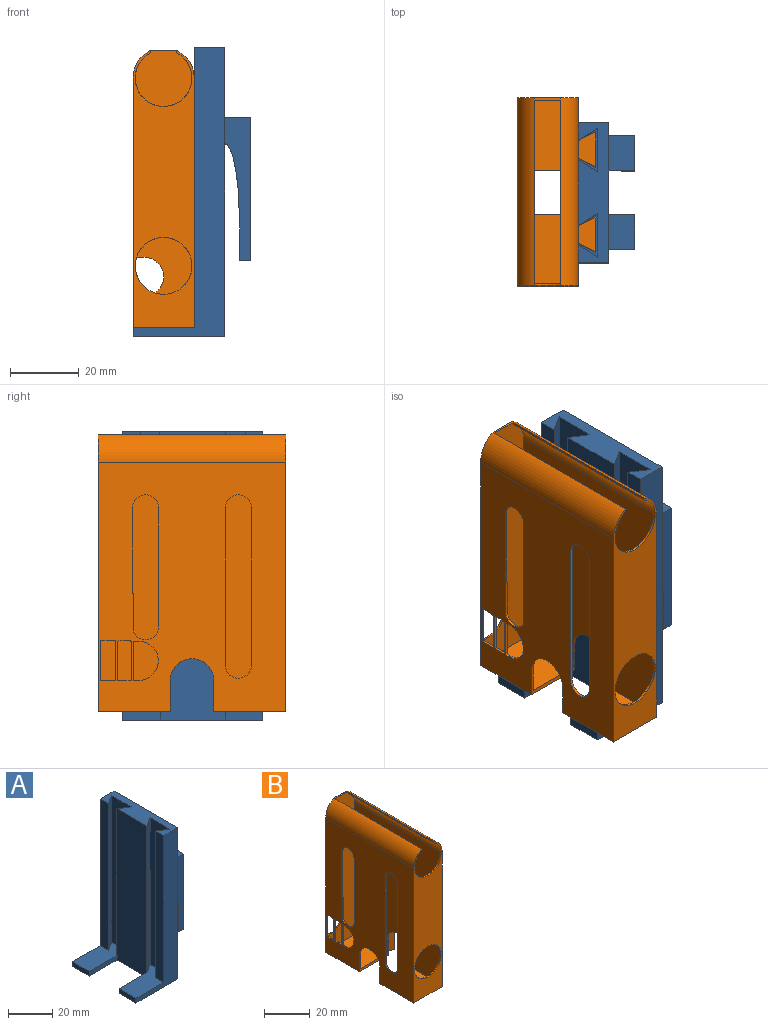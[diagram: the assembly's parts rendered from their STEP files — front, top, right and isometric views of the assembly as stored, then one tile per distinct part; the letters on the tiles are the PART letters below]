
ASSEMBLY  parts=2 mates=1
PART A: 34 faces, bbox 34.3x40.6x83.8 mm
  f0: plane 40.64x26.67mm, normal (0,0,-1), area 745.2mm2, adj f2,f5,f9,f18,f19,f20,f32,f33
  f1: plane 23.37x14.29mm, normal (0,0,1), area 243mm2, adj f2,f3,f9,f14,f15,f16,f20,f33
  f2: plane 10.8x2.54mm, normal (-1,0,0), area 27.4mm2, adj f0,f1,f20,f33
  f3: plane 81.28x5.14mm, normal (-1,0,0), area 418.1mm2, adj f1,f4,f14,f33
  f4: plane 40.64x8.89mm, normal (0,0,1), area 259.1mm2, adj f3,f5,f9,f10,f11,f12,f13,f14
  f5: plane 83.82x40.64mm, normal (1,0,0), area 3251.7mm2, adj f0,f4,f6,f7,f8,f21,f22,f24
  f6: plane 41.59x7.62mm, normal (0,1,0), area 190.3mm2, adj f5,f21,f23,f29,f30,f31
  f7: plane 41.59x7.62mm, normal (0,-1,0), area 190.3mm2, adj f5,f24,f25,f26,f27,f28
  f8: plane 41.59x7.62mm, normal (0,1,0), area 190.3mm2, adj f5,f24,f25,f26,f27,f28
  f9: plane 83.82x19.18mm, normal (-1,0,0), area 1607.1mm2, adj f0,f1,f4,f13,f15,f17,f19,f20
  f10: plane 81.28x5.14mm, normal (-1,0,0), area 418.1mm2, adj f4,f11,f17,f32
  f11: plane 81.28x5.59mm, normal (0.54,0.84,0), area 538.4mm2, adj f4,f10,f12,f17
  f12: plane 81.28x12.7mm, normal (-1,0,0), area 1032.3mm2, adj f4,f11,f13,f17
  f13: plane 81.28x5.59mm, normal (0.54,-0.84,0), area 538.4mm2, adj f4,f9,f12,f17
  f14: plane 81.28x5.59mm, normal (0.54,-0.84,0), area 538.4mm2, adj f1,f3,f4,f16
  f15: plane 81.28x5.59mm, normal (0.54,0.84,0), area 538.4mm2, adj f1,f4,f9,f16
  f16: plane 81.28x12.7mm, normal (-1,0,0), area 1032.3mm2, adj f1,f4,f14,f15
  f17: plane 23.37x14.29mm, normal (0,0,1), area 243mm2, adj f9,f10,f11,f12,f13,f18,f19,f32
  f18: plane 10.8x2.54mm, normal (-1,0,0), area 27.4mm2, adj f0,f17,f19,f32
  f19: plane 17.78x2.54mm, normal (0,1,0), area 45.2mm2, adj f0,f9,f17,f18
  f20: plane 17.78x2.54mm, normal (0,-1,0), area 45.2mm2, adj f0,f1,f2,f9
  f21: plane 10.16x7.62mm, normal (0,0,1), area 77.4mm2, adj f5,f6,f22,f23
  f22: plane 41.59x7.62mm, normal (0,-1,0), area 190.3mm2, adj f5,f21,f23,f29,f30,f31
  f23: plane 41.59x10.16mm, normal (1,0,0), area 422.6mm2, adj f6,f21,f22,f29
  f24: plane 10.16x7.62mm, normal (0,0,1), area 77.4mm2, adj f5,f7,f8,f25
  f25: plane 41.59x10.16mm, normal (1,0,0), area 422.6mm2, adj f7,f8,f24,f28
  f26: extruded ~24.13x10.16mm, area 255.8mm2, adj f5,f7,f8,f27
  f27: plane 10.16x9.84mm, normal (-1,0,0), area 100mm2, adj f7,f8,f26,f28
  f28: plane 10.16x3.22mm, normal (0,0,-1), area 32.7mm2, adj f7,f8,f25,f27
  f29: plane 10.16x3.22mm, normal (0,0,-1), area 32.7mm2, adj f6,f22,f23,f30
  f30: plane 10.16x9.84mm, normal (-1,0,0), area 100mm2, adj f6,f22,f29,f31
  f31: extruded ~24.13x10.16mm, area 255.8mm2, adj f5,f6,f22,f30
  f32: plane 83.82x26.67mm, normal (0,-1,0), area 790.3mm2, adj f0,f4,f5,f10,f17,f18
  f33: plane 83.82x26.67mm, normal (0,1,0), area 790.3mm2, adj f0,f1,f2,f3,f4,f5
PART B: 58 faces, bbox 22.9x54.6x80.4 mm
  f0: plane 72.39x54.61mm, normal (-1,0,0), area 2911mm2, adj f1,f2,f3,f4,f6,f7,f8,f9
  f1: plane 3.89x0.64mm, normal (0,0,1), area 2.5mm2, adj f0,f13,f51,f54
  f2: plane 1.56x0.64mm, normal (0,0,-1), area 1mm2, adj f0,f13,f47,f55
  f3: cylinder r=3.81mm len=7.42mm, axis (-1,0,0), area 6.8mm2, adj f0,f7,f13,f52
  f4: plane 4.45x0.64mm, normal (0,0,1), area 2.8mm2, adj f0,f13,f48,f50
  f5: plane 2.54x0.64mm, normal (0,0,1), area 1.6mm2, adj f11,f19,f35,f49
  f6: plane 24.77x0.64mm, normal (0,-1,0), area 15.7mm2, adj f0,f13,f30,f53
  f7: plane 34.5x0.64mm, normal (0,1,0), area 21.9mm2, adj f0,f3,f13,f30
  f8: plane 22.86x20.96mm, normal (0,0,-1), area 411.3mm2, adj f0,f10,f21,f33,f40,f45,f46
  f9: plane 22.86x20.96mm, normal (0,0,-1), area 411.3mm2, adj f0,f10,f11,f32,f42,f43,f44
  f10: plane 72.39x54.61mm, normal (1,0,0), area 3157.6mm2, adj f8,f9,f11,f21,f23,f32,f33,f38
  f11: plane 80.42x17.78mm, normal (0,1,0), area 1326.5mm2, adj f0,f5,f9,f10,f23,f24,f25,f34
  f12: plane 71.12x53.34mm, normal (-1,0,0), area 3633.4mm2, adj f14,f15,f17,f19,f20,f22,f32,f33
  f13: plane 71.12x53.34mm, normal (1,0,0), area 2767.5mm2, adj f1,f2,f3,f4,f6,f7,f14,f15
  f14: plane 20.32x16.51mm, normal (0,0,1), area 335.5mm2, adj f12,f13,f19,f32
  f15: plane 54.61x16.51mm, normal (0,1,0), area 687.5mm2, adj f12,f13,f17,f31
  f16: plane 53.98x0.71mm, normal (-1,0,0), area 38.3mm2, adj f17,f19,f21,f23
  f17: cylinder r=8.26mm len=53.98mm, axis (0,-1,0), area 988.7mm2, adj f12,f13,f15,f16,f18,f19,f21
  f18: plane 53.98x0.71mm, normal (1,0,0), area 38.3mm2, adj f17,f19,f21,f24
  f19: plane 79.15x16.51mm, normal (0,-1,0), area 1201.5mm2, adj f5,f12,f13,f14,f16,f17,f18,f25
  f20: plane 16.51x16.51mm, normal (0,1,0), area 165.5mm2, adj f12,f13,f22,f31
  f21: plane 80.42x17.78mm, normal (0,-1,0), area 978.1mm2, adj f0,f8,f10,f16,f17,f18,f23,f24
  f22: plane 20.32x16.51mm, normal (0,0,1), area 335.5mm2, adj f12,f13,f20,f33
  f23: cylinder r=8.89mm len=54.61mm, axis (0,-1,0), area 547.6mm2, adj f10,f11,f16,f21,f25
  f24: cylinder r=8.89mm len=54.61mm, axis (0,-1,0), area 547.6mm2, adj f0,f11,f18,f21,f25
  f25: plane 7.62x0.64mm, normal (0,0,1), area 4.8mm2, adj f11,f19,f23,f24
  f26: cylinder r=3.81mm len=7.62mm, axis (-1,0,0), area 7.6mm2, adj f0,f13,f27,f29
  f27: plane 45.72x0.64mm, normal (0,1,0), area 29mm2, adj f0,f13,f26,f28
  f28: cylinder r=3.81mm len=7.62mm, axis (-1,0,0), area 7.6mm2, adj f0,f13,f27,f29
  f29: plane 45.72x0.64mm, normal (0,-1,0), area 29mm2, adj f0,f13,f26,f28
  f30: cylinder r=3.81mm len=7.62mm, axis (-1,0,0), area 7.6mm2, adj f0,f6,f7,f13
  f31: cylinder r=8.26mm len=16.51mm, axis (0,-1,0), area 32.9mm2, adj f15,f20,f21
  f32: plane 17.78x8.89mm, normal (0,-1,0), area 32.3mm2, adj f0,f9,f10,f12,f13,f14,f37,f38
  f33: plane 17.78x8.89mm, normal (0,1,0), area 32.3mm2, adj f0,f8,f10,f12,f13,f22,f37,f38
  f34: plane 2.54x0.64mm, normal (0,0,-1), area 1.6mm2, adj f11,f19,f35,f49
  f35: cylinder r=5.71mm len=11.43mm, axis (0,1,0), area 11.4mm2, adj f5,f11,f19,f34
  f36: plane 1.56x0.64mm, normal (0,0,1), area 1mm2, adj f0,f13,f47,f55
  f37: cylinder r=6.35mm len=12.7mm, axis (1,0,0), area 12.7mm2, adj f0,f13,f32,f33
  f38: cylinder r=6.35mm len=12.7mm, axis (1,0,0), area 12.7mm2, adj f10,f12,f32,f33
  f39: plane 10.16x5.08mm, normal (0,0,1), area 38.7mm2, adj f10,f40,f45,f46
  f40: plane 60.96x10.16mm, normal (1,0,0), area 619.4mm2, adj f8,f39,f45,f46
  f41: plane 10.16x5.08mm, normal (0,0,1), area 38.7mm2, adj f10,f42,f43,f44
  f42: plane 60.96x10.16mm, normal (1,0,0), area 619.4mm2, adj f9,f41,f43,f44
  f43: plane 60.96x5.08mm, normal (-0.45,-0.89,0), area 346.2mm2, adj f9,f10,f41,f42
  f44: plane 60.96x5.08mm, normal (-0.45,0.89,0), area 346.2mm2, adj f9,f10,f41,f42
  f45: plane 60.96x5.08mm, normal (-0.45,-0.89,0), area 346.2mm2, adj f8,f10,f39,f40
  f46: plane 60.96x5.08mm, normal (-0.45,0.89,0), area 346.2mm2, adj f8,f10,f39,f40
  f47: cylinder r=5.71mm len=11.43mm, axis (-1,0,0), area 11.4mm2, adj f0,f2,f13,f36
  f48: plane 11.43x0.64mm, normal (0,-1,0), area 7.3mm2, adj f0,f4,f49,f57
  f49: plane 11.43x0.64mm, normal (1,0,0), area 7.3mm2, adj f5,f11,f34,f48
  f50: plane 11.43x0.64mm, normal (0,1,0), area 7.3mm2, adj f0,f4,f13,f57
  f51: plane 11.43x0.64mm, normal (0,-1,0), area 7.3mm2, adj f0,f1,f13,f56
  f52: plane 10.96x0.64mm, normal (0,-1,0), area 7mm2, adj f0,f3,f13,f53
  f53: plane 0.64x0.2mm, normal (0,0,1), area 0.1mm2, adj f0,f6,f13,f52
  f54: plane 11.43x0.64mm, normal (0,1,0), area 7.3mm2, adj f0,f1,f13,f56
  f55: plane 11.43x0.64mm, normal (0,-1,0), area 7.3mm2, adj f0,f2,f13,f36
  f56: extruded ~3.89x0.64mm, area 2.5mm2, adj f0,f13,f51,f54
  f57: extruded ~4.45x0.64mm, area 2.9mm2, adj f0,f13,f48,f50
PLACE A t=(2.85,16.61,-18.2)mm fixed
PLACE B t=(-14.93,16.87,-18.09)mm
MATE slider B.f41 <-> A.f4  axis (0,0,1) through (-6.04,31.79,42.87)mm
